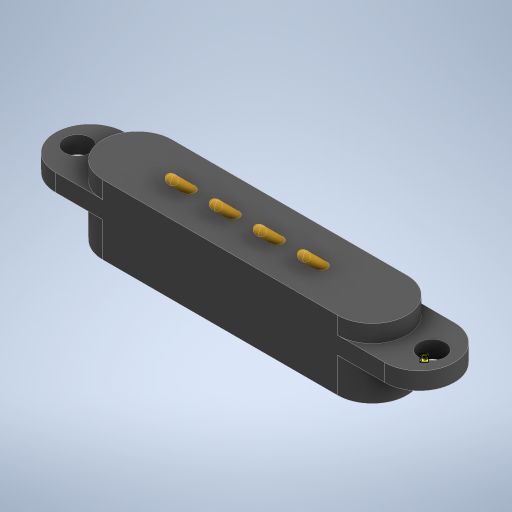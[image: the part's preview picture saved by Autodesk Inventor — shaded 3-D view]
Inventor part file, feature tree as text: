
AUTODESK INVENTOR PART (.ipt)
format: ipt  version: 2023 (Build 270158000, 158)  size: 1,014,784 bytes
history: native  units: mm
features: projected_geometry x8, sketch x7, extrude x5, plane x1, sweep x1, fillet x1, other x1
ambient origin geometry x8: Origin, YZ Plane, XZ Plane, XY Plane, X Axis, Y Axis, Z Axis, Center Point
bodies: Solid1 (feature_tree)
feature tree (24):
  extrude  "Extrusion1"  Depth=4.0mm
  extrude  "Extrusion2"  Depth=4.0mm
  extrude  "Extrusion3"  Depth=1.5mm
  sketch  "Sketch4"  dims[d26=20.44mm d27=1.0mm d28=0.0mm]
  extrude  "Extrusion6"  Depth=1.0mm TaperAngle=0.0deg
  extrude  "Extrusion7"  Depth=2.54mm
  sketch  "Sketch7"  dims[d33=7.62mm d34=1.51mm d41=3.0mm]
  plane  "Work Plane2"
  sweep  "Sweep1"
  fillet  "Fillet2"  Radius=3.0mm
  sketch  "Sketch1"  dims[d11=17.54mm d18=4.0mm]
  other  "Image1"
  sketch  "Sketch2"  dims[d21=2.0mm d22=0.0mm d23=4.0mm]
  projected_geometry  "Projected Loop1"
  sketch  "Sketch3"  dims[d24=23.0mm d25=1.5mm]
  projected_geometry  "Projected Loop2"
  sketch  "Sketch6"  dims[d30=1.0mm d31=0.0mm d32=2.54mm]
  projected_geometry  "Projected Loop6"
  projected_geometry  "Projected Loop7"
  projected_geometry  "Projected Loop8"
  projected_geometry  "Projected Loop9"
  projected_geometry  "Projected Loop10"
  projected_geometry  "Projected Loop11"
  sketch  "Sketch8"  dims[d42=0.1mm d43=0.0mm d44=0.1mm d45=0.0mm d46=0.5mm d47=0.7mm d48=1.7mm d49=45.0deg d50=0.0mm d51=0.0mm d52=0.24mm]
